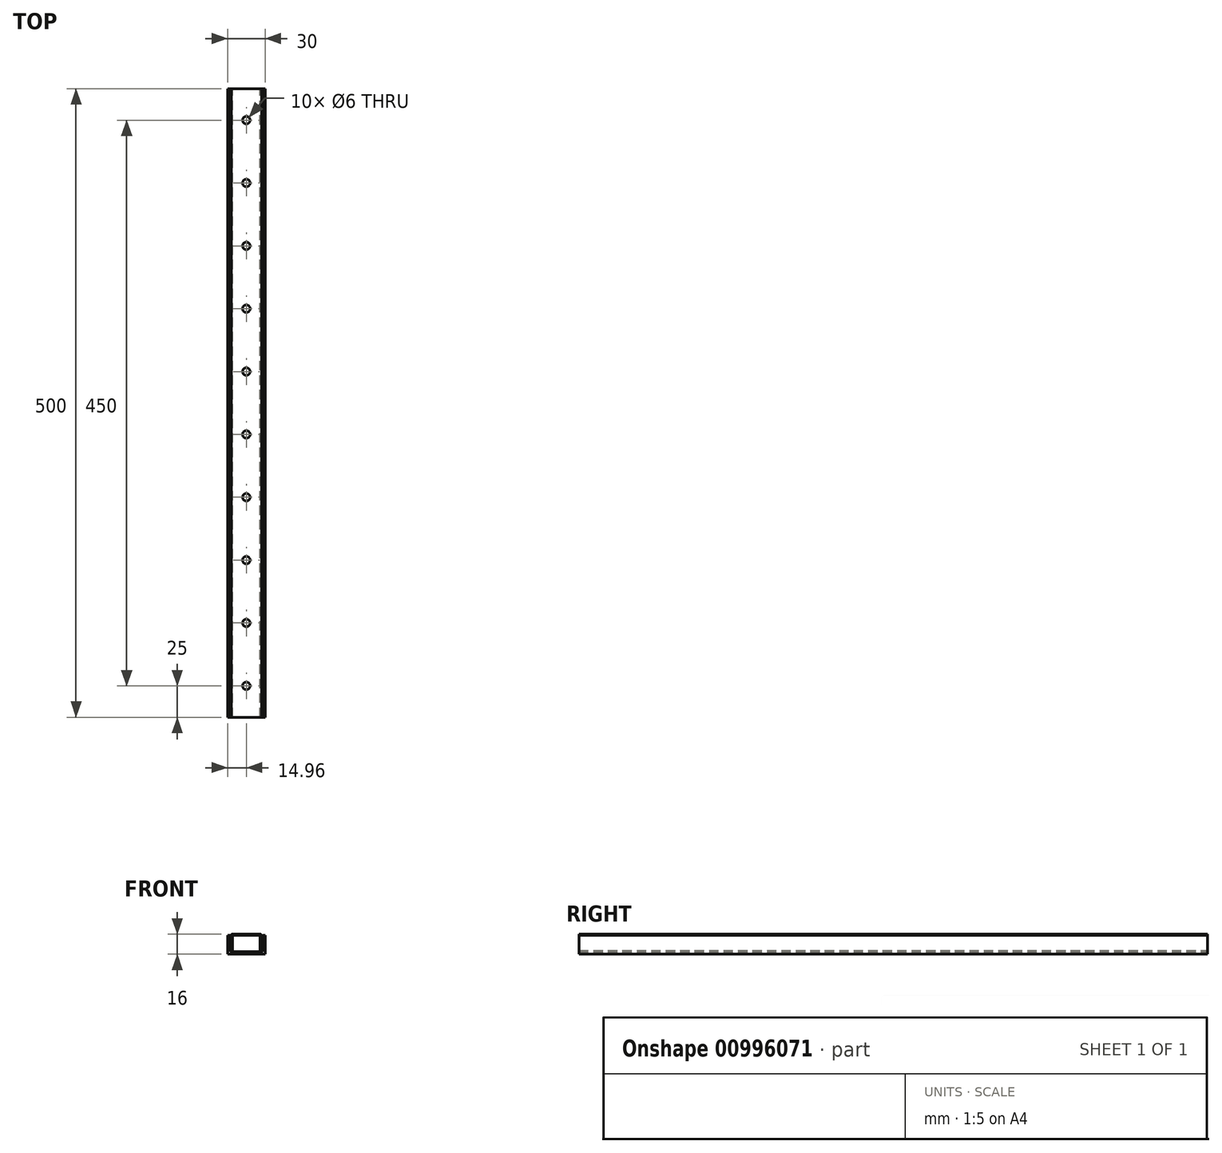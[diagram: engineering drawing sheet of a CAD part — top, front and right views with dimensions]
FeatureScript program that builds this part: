
annotation { "Feature Type Name" : "Feature", "Feature Type Description" : "" }
export const myFeature = defineFeature(function(context is Context, id is Id, definition is map)
    precondition{}
    {
        {
            var Q0;
            Q0=qCreatedBy(makeId("Front.planeOp"),FACE);
            var sketch = newSketch(context, id + "F0", { "sketchPlane" : qUnion([Q0])});
            skLineSegment(sketch, "E0.bottom", {"start": v(15, 7.5) * mm, "end": v(-15, 7.5) * mm});
            skLineSegment(sketch, "E0.top", {"start": v(15, -7.5) * mm, "end": v(-15, -7.5) * mm});
            skLineSegment(sketch, "E0.left", {"start": v(15, 7.5) * mm, "end": v(15, -7.5) * mm});
            skLineSegment(sketch, "E0.right", {"start": v(-15, 7.5) * mm, "end": v(-15, -7.5) * mm});
            skPoint(sketch, "E0.middle", {"position": v(0, 0) * mm});
            skSolve(sketch);
        }
        {
            var Q0;
            Q0=makeQuery(id+"F0.imprint","IMPRINT",FACE,{"disambiguationData":[TD([[makeQuery(id+"F0.imprint","IMPRINT",EDGE,{"derivedFrom":sQuery(id+"F0.wireOp",EDGE,"E0.bottom")}),1.0]])]});
            var sketch = newSketch(context, id + "F1", { "sketchPlane" : qUnion([Q0])});
            skLineSegment(sketch, "E1.bottom", {"start": v(-13, 7.5) * mm, "end": v(13, 7.5) * mm});
            skLineSegment(sketch, "E1.top", {"start": v(-13, -5.5) * mm, "end": v(13, -5.5) * mm});
            skLineSegment(sketch, "E1.left", {"start": v(-13, 7.5) * mm, "end": v(-13, -5.5) * mm});
            skLineSegment(sketch, "E1.right", {"start": v(13, 7.5) * mm, "end": v(13, -5.5) * mm});
            skSolve(sketch);
        }
        {
            var Q0;
            Q0 = qSketchRegion(id + "F0", true);
            extrude(context, id + "F2", {"entities" : qUnion([Q0]), "endBound" : BoundingType.SYMMETRIC, "depth" : 500 * mm, "offsetDistance" : 25 * mm});
        }
        {
            var Q0;
            Q0 = qSketchRegion(id + "F1", true);
            extrude(context, id + "F3", {"entities" : qUnion([Q0]), "operationType" : NewBodyOperationType.REMOVE, "endBound" : BoundingType.SYMMETRIC, "depth" : 600 * mm, "offsetDistance" : 25 * mm});
        }
        {
            var Q0;
            Q0=qCreatedBy(makeId("Front.planeOp"),FACE);
            var sketch = newSketch(context, id + "F4", { "sketchPlane" : qUnion([Q0])});
            skLineSegment(sketch, "E2.bottom", {"start": v(-12.08, -4.5) * mm, "end": v(12, -4.5) * mm});
            skLineSegment(sketch, "E2.top", {"start": v(-11.08, 8.5) * mm, "end": v(11, 8.5) * mm});
            skLineSegment(sketch, "E2.left", {"start": v(-12.08, -4.5) * mm, "end": v(-12.08, 7.5) * mm});
            skLineSegment(sketch, "E2.right", {"start": v(12, -4.5) * mm, "end": v(12, 7.5) * mm});
            skPoint(sketch, "E3.visualSharp", {"position": v(12, 8.5) * mm});
            skArc(sketch, "E3.filletArc", {"start": v(12, 7.5) * mm, "mid": v(11.7, 8.2) * mm, "end": v(11, 8.5) * mm});
            skPoint(sketch, "E4.visualSharp", {"position": v(-12.08, 8.5) * mm});
            skArc(sketch, "E4.filletArc", {"start": v(-11.08, 8.5) * mm, "mid": v(-11.79, 8.2) * mm, "end": v(-12.08, 7.5) * mm});
            skSolve(sketch);
        }
        {
            var Q0;
            Q0=makeQuery(id+"F4.imprint","IMPRINT",FACE,{"disambiguationData":[TD([[makeQuery(id+"F4.imprint","IMPRINT",EDGE,{"derivedFrom":sQuery(id+"F4.wireOp",EDGE,"E2.bottom")}),1.0]])]});
            var sketch = newSketch(context, id + "F5", { "sketchPlane" : qUnion([Q0])});
            skLineSegment(sketch, "E5.bottom", {"start": v(-11.08, 7.5) * mm, "end": v(11, 7.5) * mm});
            skLineSegment(sketch, "E5.top", {"start": v(-11.08, -4.5) * mm, "end": v(11, -4.5) * mm});
            skLineSegment(sketch, "E5.left", {"start": v(-11.08, 7.5) * mm, "end": v(-11.08, -4.5) * mm});
            skLineSegment(sketch, "E5.right", {"start": v(11, 7.5) * mm, "end": v(11, -4.5) * mm});
            skSolve(sketch);
        }
        {
            var Q0;
            Q0 = qSketchRegion(id + "F4", true);
            extrude(context, id + "F6", {"entities" : qUnion([Q0]), "endBound" : BoundingType.SYMMETRIC, "depth" : 500 * mm, "offsetDistance" : 25 * mm});
        }
        {
            var Q0;
            Q0 = qSketchRegion(id + "F5", true);
            extrude(context, id + "F7", {"entities" : qUnion([Q0]), "operationType" : NewBodyOperationType.REMOVE, "endBound" : BoundingType.SYMMETRIC, "depth" : 600 * mm, "offsetDistance" : 25 * mm});
        }
        {
            var Q0;
            Q0=makeQuery(id+"F6.opExtrude","SWEPT_FACE",FACE,{"disambiguationData":[OSD([sQuery(id+"F4.wireOp",EDGE,"E2.top")])]});
            var sketch = newSketch(context, id + "F8", { "sketchPlane" : qUnion([Q0])});
            skPoint(sketch, "E6", {"position": v(-0.04, -225) * mm});
            skPoint(sketch, "E6.positionSnap0", {"position": v(-0.04, -250) * mm});
            skPoint(sketch, "E7.0.1.0", {"position": v(-0.04, -175) * mm});
            skPoint(sketch, "E7.0.2.0", {"position": v(-0.04, -125) * mm});
            skPoint(sketch, "E7.0.3.0", {"position": v(-0.04, -75) * mm});
            skPoint(sketch, "E7.0.4.0", {"position": v(-0.04, -25) * mm});
            skPoint(sketch, "E7.0.5.0", {"position": v(-0.04, 25) * mm});
            skPoint(sketch, "E7.0.6.0", {"position": v(-0.04, 75) * mm});
            skPoint(sketch, "E7.0.7.0", {"position": v(-0.04, 125) * mm});
            skPoint(sketch, "E7.0.8.0", {"position": v(-0.04, 175) * mm});
            skPoint(sketch, "E7.0.9.0", {"position": v(-0.04, 225) * mm});
            skLineSegment(sketch, "E7.direction2", {"start": v(-0.04, -250) * mm, "end": v(-0.04, 250) * mm, "construction": true});
            skSolve(sketch);
        }
        {
            var Q0;
            Q0=sQuery(id+"F8.wireOp",VERTEX,"E6");
            var Q1;
            Q1=sQuery(id+"F8.wireOp",VERTEX,"E7.0.1.0");
            var Q2;
            Q2=sQuery(id+"F8.wireOp",VERTEX,"E7.0.2.0");
            var Q3;
            Q3=sQuery(id+"F8.wireOp",VERTEX,"E7.0.3.0");
            var Q4;
            Q4=sQuery(id+"F8.wireOp",VERTEX,"E7.0.4.0");
            var Q5;
            Q5=sQuery(id+"F8.wireOp",VERTEX,"E7.0.5.0");
            var Q6;
            Q6=sQuery(id+"F8.wireOp",VERTEX,"E7.0.6.0");
            var Q7;
            Q7=sQuery(id+"F8.wireOp",VERTEX,"E7.0.7.0");
            var Q8;
            Q8=sQuery(id+"F8.wireOp",VERTEX,"E7.0.8.0");
            var Q9;
            Q9=sQuery(id+"F8.wireOp",VERTEX,"E7.0.9.0");
            var Q10;
            Q10=makeQuery(id+"F6.opExtrude","SWEPT_BODY",BODY,{"disambiguationData":[OSD([sQuery(id+"F4.wireOp",EDGE,"E2.bottom"),sQuery(id+"F4.wireOp",EDGE,"E2.top"),sQuery(id+"F4.wireOp",EDGE,"E2.left"),sQuery(id+"F4.wireOp",EDGE,"E2.right")])]});
            hole(context, id + "F9", {"style" : HoleStyle.SIMPLE, "endStyle" : HoleEndStyle.THROUGH, "standardTappedOrClearance" : lookupTablePath({ "standard" : "ISO", "size" : "6", "type" : "Drilled" }), "standardBlindInLast" : lookupTablePath({ "standard" : "ISO", "size" : "6", "type" : "Drilled" }), "holeDiameter" : 6 * mm, "majorDiameter" : 5 * mm, "isTappedThrough" : true, "tappedDepth" : 12 * mm, "tapClearance" : 3, "locations" : qUnion([Q0, Q1, Q2, Q3, Q4, Q5, Q6, Q7, Q8, Q9]), "scope" : qUnion([Q10])});
        }
    });
